# Revit family: Reece_Toilet_Posh_Solus_Round Link
name_source: partatom
category: Plumbing Fixtures
revit_build: Autodesk Revit 2018 (Build: 20180329_1100(x64)
units: mm (PartAtom-declared; Revit-internal decimal feet)

## family parameters
Always vertical = Yes
Cut with Voids When Loaded = No
Part Type = Normal
Room Calculation Point = No
Round Connector Dimension = Use Diameter
Shared = No
Work Plane-Based = No

## types (1)
- Soft Close Seat and Link Piece_Bottom Inlet_White
    Description = Posh Solus Round Link Toilet Suite S Trap with Soft Close Seat White/ Chrome (4 Star)
    Disclaimer = THIS FILE IS THE PROPERTY OF THE REECE GROUP. IT MAY NOT BE REPRODUCED, REVERSE-ENGINEERED OR MODIFIED. ANY REPUBLICATION, TRANSMISSION OR DISTRIBUTION FOR THE PURPOSE OF COMMERCIALLY EXPLOITING THE FILES IS PROHIBITED.
    Keynote = Product #9502975, Reece_Toilet_Posh_Solus_Round Link - Soft Close Seat and Link Piece_Bottom Inlet_White
    Manufacturer = Posh
    Model = Solus
    Reece_Back-Inlet = 0 mm  [stored 0 ft]
    Reece_Bottom-Inlet = 30 mm  [stored 0.0984252 ft]
    Reece_Detail_Additional = Box Rim
    Reece_Detail_Connector = S Trap
    Reece_Detail_Disclaimer = THIS FILE IS THE PROPERTY OF THE REECE GROUP. IT MAY NOT BE REPRODUCED, REVERSE-ENGINEERED OR MODIFIED. ANY REPUBLICATION, TRANSMISSION OR DISTRIBUTION FOR THE PURPOSE OF COMMERCIALLY EXPLOITING THE FILES IS PROHIBITED.
    Reece_Material-Cistern = Reece_Vitreous China_White
    Reece_Material-Seat = Reece_Acrylic_White
    Reece_Material-Secondary = Reece_Brass_Chrome
    Reece_Material_Main = Reece_Vitreous China_White
    Reece_Overall-Height = 880 mm  [stored 2.88714 ft]
    Reece_Overall-Width = 375 mm  [stored 1.23031 ft]
    Reece_Overall_Length = 670 mm  [stored 2.19816 ft]
    Reece_P-Trap = 0 mm  [stored 0 ft]
    Reece_Product_Brand = Posh
    Reece_Product_Description = Posh Solus Round Link Toilet Suite S Trap with Soft Close Seat White (4 Star)
    Reece_Product_Mount = Floor Mounted
    Reece_Product_Number = 9502975
    Reece_Product_Sub Brand = Solus
    Reece_Product_Type = Toilet
    Reece_Product_Web Page = https://www.reece.com.au
    Reece_S-Trap = 102 mm
    Reece_Seat-Height = 410 mm
    Reece_Seat-Visibility = Yes
    URL = https://www.reece.com.au

note: [stored X ft] marks values corroborated as IEEE doubles in the binary element streams (Revit-internal decimal feet)

## geometry (parser evidence)
native form markers: Sweep x1
no freeform markers — native parametric forms only
